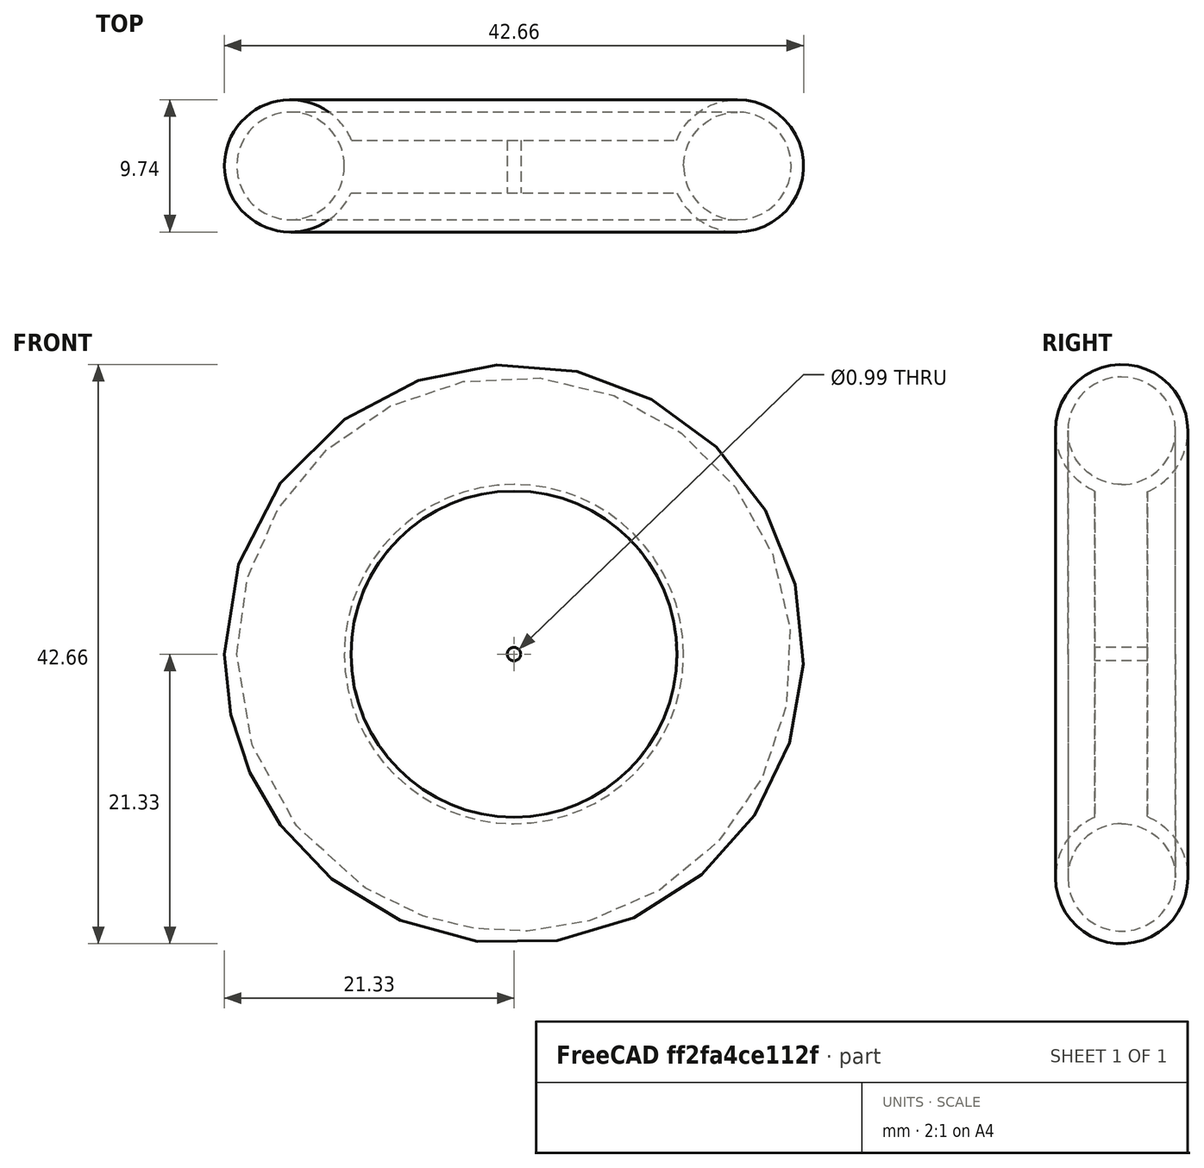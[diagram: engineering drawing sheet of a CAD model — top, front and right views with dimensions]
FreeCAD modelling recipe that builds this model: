
FCSTD DOCUMENT  (FreeCAD 0.18R16146 (Git))
Label: foot_actuator
License: All rights reserved
LicenseURL: http://en.wikipedia.org/wiki/All_rights_reserved
objects: Sketcher::SketchObject×1, PartDesign::Revolution×1, PartDesign::Body×1
note: 4 computed .brp shape members not serialized (recipe doc carries the construction recipe); baked Part::Feature solids carry a one-line shape summary decoded from their .brp

FEATURE [Sketcher::SketchObject] Sketch002
  MapMode = 5
  Support = -> [XY_Plane003]
  sketch-geometry (5):
    g0: LineSegment StartX=-0.49654 StartY=2.36587 StartZ=0 EndX=-0.49654 EndY=-1.50449 EndZ=0
    g1: LineSegment StartX=-0.49654 StartY=-1.50449 StartZ=0 EndX=-12.0035 EndY=-1.50449 EndZ=0
    g2: LineSegment StartX=-0.49654 StartY=2.36587 StartZ=0 EndX=-11.9617 EndY=2.36587 EndZ=0
    g3: ArcOfCircle CenterX=-16.4535 CenterY=0.478965 CenterZ=0 NormalX=0 NormalY=0 NormalZ=1 AngleXU=0 Radius=4.87205 StartAngle=0.397692 EndAngle=5.8639
    g4: Circle CenterX=-16.4535 CenterY=0.478965 CenterZ=0 NormalX=0 NormalY=0 NormalZ=1 AngleXU=0 Radius=3.96164
  constraints (8):
    c: Coincident(g2,g3)
    c: Coincident(g0,g2)
    c: Coincident(g1,g0)
    c: Horizontal(g1)
    c: Horizontal(g2)
    c: Vertical(g0)
    c: Coincident(g3,g1)
    c: Coincident(g3,g4)
FEATURE [PartDesign::Revolution] Revolution
  Angle = 360
  Axis = (0,1,0)
  Base = (0,0,0)
  Profile = -> Sketch002
  ReferenceAxis = -> Sketch002 [V_Axis]
FEATURE [PartDesign::Body] Body003
  Group = -> [Sketch002,Revolution]
  Origin = -> Origin003
  Tip = -> Revolution
